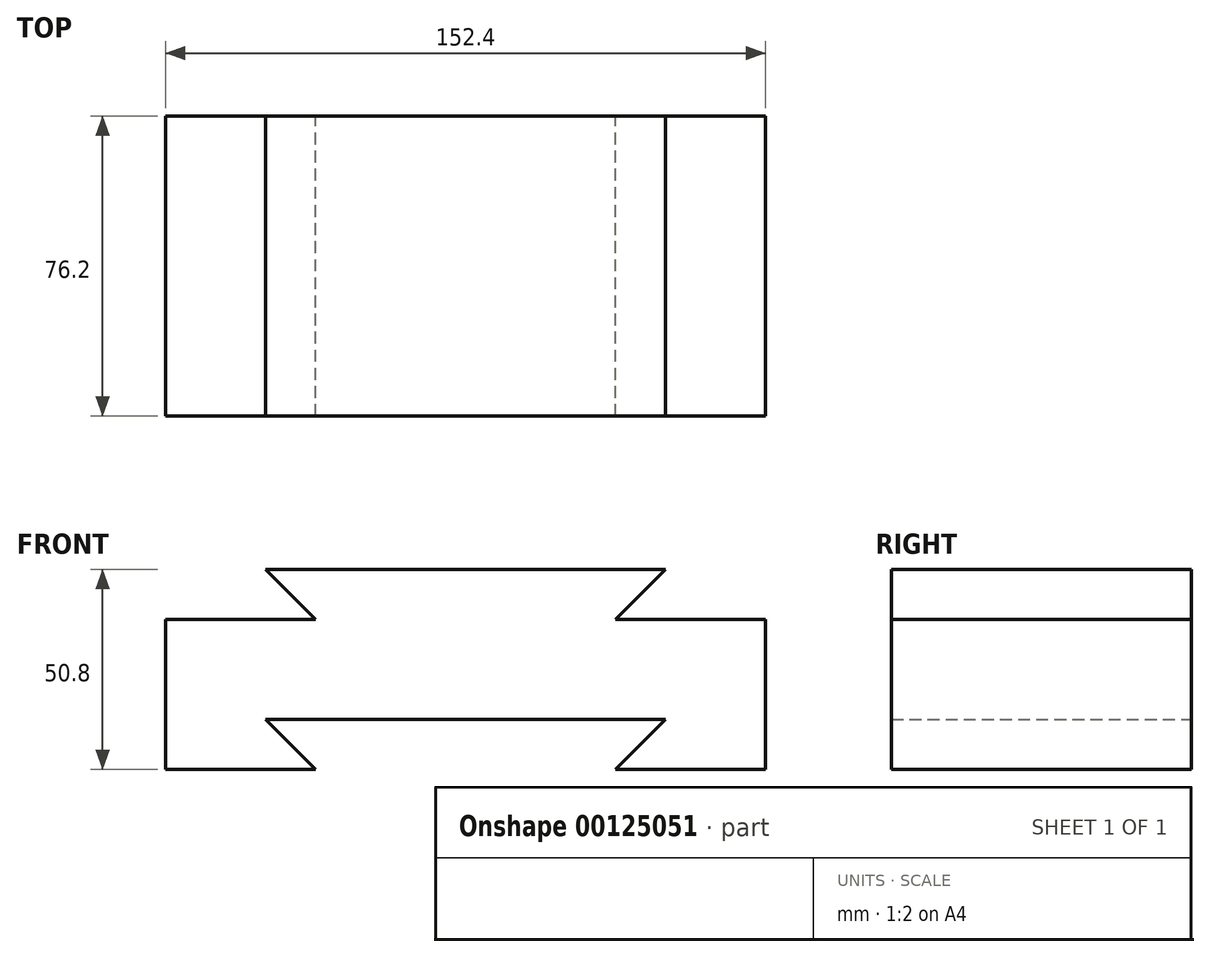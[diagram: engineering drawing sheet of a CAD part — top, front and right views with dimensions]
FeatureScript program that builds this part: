
annotation { "Feature Type Name" : "Feature", "Feature Type Description" : "" }
export const myFeature = defineFeature(function(context is Context, id is Id, definition is map)
    precondition{}
    {
        {
            var Q0;
            Q0=qCreatedBy(makeId("Front.planeOp"),FACE);
            var sketch = newSketch(context, id + "F0", { "sketchPlane" : qUnion([Q0])});
            skLineSegment(sketch, "E0.left", {"start": v(76.2, -19.05) * mm, "end": v(76.2, 19.05) * mm});
            skLineSegment(sketch, "E0.right", {"start": v(-76.2, -19.05) * mm, "end": v(-76.2, 19.05) * mm});
            skPoint(sketch, "E0.middle", {"position": v(0, 0) * mm});
            skLineSegment(sketch, "E1", {"start": v(-76.2, -19.05) * mm, "end": v(-38.1, -19.05) * mm});
            skLineSegment(sketch, "E2", {"start": v(-50.8, -6.35) * mm, "end": v(-38.1, -19.05) * mm});
            skLineSegment(sketch, "E3", {"start": v(-50.8, -6.35) * mm, "end": v(50.8, -6.35) * mm});
            skLineSegment(sketch, "E4", {"start": v(38.1, -19.05) * mm, "end": v(50.8, -6.35) * mm});
            skLineSegment(sketch, "E5", {"start": v(38.1, -19.05) * mm, "end": v(76.2, -19.05) * mm});
            skLineSegment(sketch, "E6", {"start": v(-76.2, 19.05) * mm, "end": v(-38.1, 19.05) * mm});
            skLineSegment(sketch, "E7", {"start": v(-50.8, 31.75) * mm, "end": v(-38.1, 19.05) * mm});
            skLineSegment(sketch, "E8", {"start": v(38.1, 19.05) * mm, "end": v(50.8, 31.75) * mm});
            skLineSegment(sketch, "E9", {"start": v(38.1, 19.05) * mm, "end": v(76.2, 19.05) * mm});
            skLineSegment(sketch, "E10", {"start": v(-50.8, 31.75) * mm, "end": v(50.8, 31.75) * mm});
            skSolve(sketch);
        }
        {
            var Q0;
            Q0 = qSketchRegion(id + "F0", true);
            extrude(context, id + "F1", {"entities" : qUnion([Q0]), "endBound" : BoundingType.SYMMETRIC, "depth" : 76.2 * mm});
        }
    });
